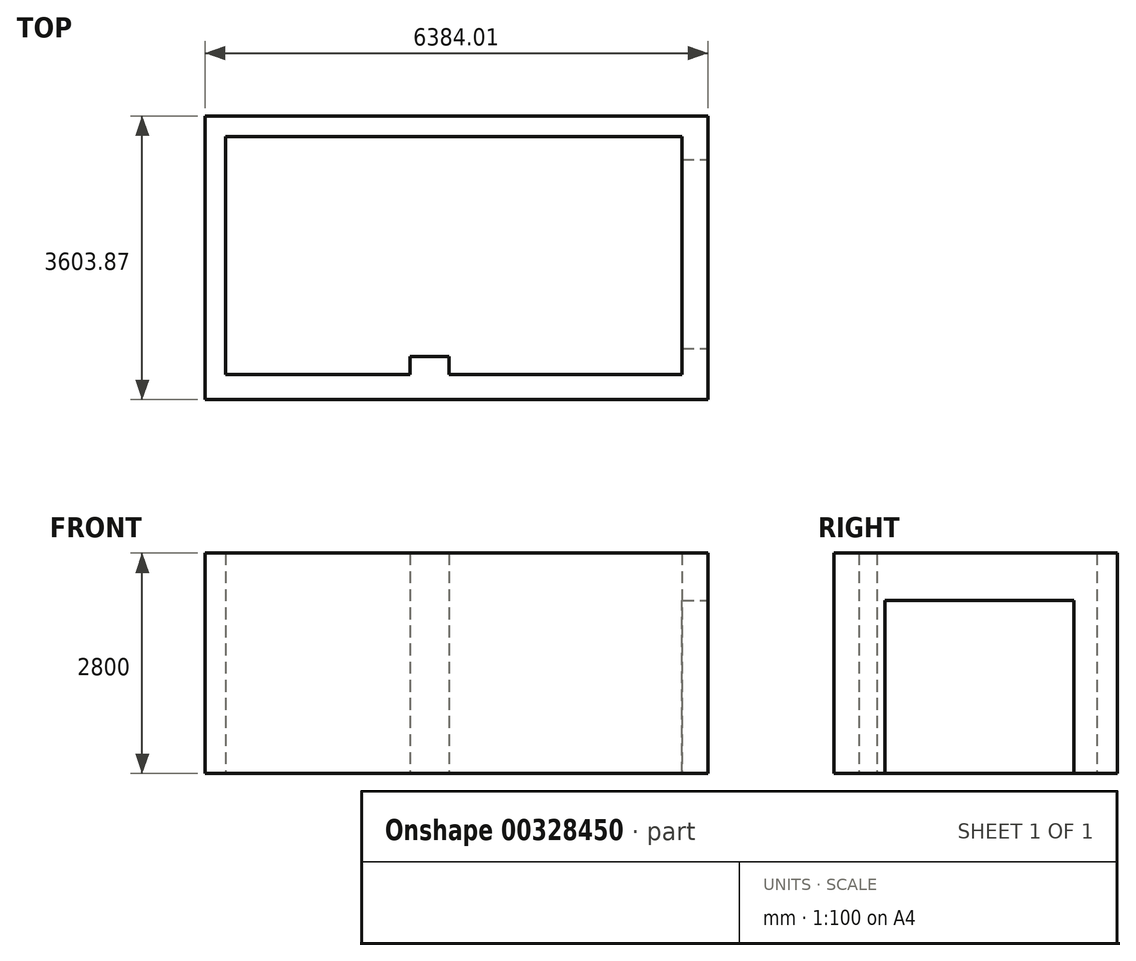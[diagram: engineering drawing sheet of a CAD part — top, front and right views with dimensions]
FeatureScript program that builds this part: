
annotation { "Feature Type Name" : "Feature", "Feature Type Description" : "" }
export const myFeature = defineFeature(function(context is Context, id is Id, definition is map)
    precondition{}
    {
        {
            var Q0;
            Q0=qCreatedBy(makeId("Top.planeOp"),FACE);
            var sketch = newSketch(context, id + "F0", { "sketchPlane" : qUnion([Q0])});
            skLineSegment(sketch, "E0.bottom", {"start": v(-2841.03, -1497.18) * mm, "end": v(-498.77, -1497.18) * mm});
            skLineSegment(sketch, "E0.top", {"start": v(-2841.03, 1522.82) * mm, "end": v(2958.97, 1522.82) * mm});
            skLineSegment(sketch, "E0.left", {"start": v(-2841.03, -1497.18) * mm, "end": v(-2841.03, 1522.82) * mm});
            skLineSegment(sketch, "E0.right", {"start": v(2958.97, -1497.18) * mm, "end": v(2958.97, 1522.82) * mm});
            skLineSegment(sketch, "E1", {"start": v(-498.77, -1497.18) * mm, "end": v(-498.77, -1267.18) * mm});
            skLineSegment(sketch, "E2", {"start": v(-498.77, -1267.18) * mm, "end": v(1.23, -1267.18) * mm});
            skLineSegment(sketch, "E3", {"start": v(1.23, -1267.18) * mm, "end": v(1.23, -1497.18) * mm});
            skLineSegment(sketch, "E4.trimOffspring", {"start": v(1.23, -1497.18) * mm, "end": v(2958.97, -1497.18) * mm});
            skLineSegment(sketch, "E5.bottom", {"start": v(-3098.2, 1787.07) * mm, "end": v(3285.8, 1787.07) * mm});
            skLineSegment(sketch, "E5.top", {"start": v(-3098.2, -1816.8) * mm, "end": v(3285.8, -1816.8) * mm});
            skLineSegment(sketch, "E5.left", {"start": v(-3098.2, 1787.07) * mm, "end": v(-3098.2, -1816.8) * mm});
            skLineSegment(sketch, "E5.right", {"start": v(3285.8, 1787.07) * mm, "end": v(3285.8, -1816.8) * mm});
            skSolve(sketch);
        }
        {
            var Q0;
            Q0 = qSketchRegion(id + "F0", true);
            extrude(context, id + "F1", {"entities" : qUnion([Q0]), "depth" : 2800 * mm});
        }
        {
            var Q0;
            Q0=makeQuery(id+"F1.opExtrude","SWEPT_FACE",FACE,{"disambiguationData":[OSD([sQuery(id+"F0.wireOp",EDGE,"E5.right")])]});
            var sketch = newSketch(context, id + "F2", { "sketchPlane" : qUnion([Q0])});
            skLineSegment(sketch, "E6.bottom", {"start": v(-1166.8, 0) * mm, "end": v(1233.2, 0) * mm});
            skLineSegment(sketch, "E6.top", {"start": v(-1166.8, 2200) * mm, "end": v(1233.2, 2200) * mm});
            skLineSegment(sketch, "E6.left", {"start": v(-1166.8, 0) * mm, "end": v(-1166.8, 2200) * mm});
            skLineSegment(sketch, "E6.right", {"start": v(1233.2, 0) * mm, "end": v(1233.2, 2200) * mm});
            skSolve(sketch);
        }
        {
            var Q0;
            Q0 = qSketchRegion(id + "F2", true);
            extrude(context, id + "F3", {"entities" : qUnion([Q0]), "operationType" : NewBodyOperationType.REMOVE, "endBound" : BoundingType.UP_TO_NEXT, "oppositeDirection" : true, "depth" : 25 * mm});
        }
    });
